# Revit family: Lighting_Pendants_Zero_Sprinkle
name_source: partatom
category: Lighting Fixtures
units: mm (PartAtom-declared; Revit-internal decimal feet)

## family parameters
Always vertical = Yes
Cut with Voids When Loaded = No
Light Source = Yes
OmniClass Number = 23.80.70.00
OmniClass Title = Lighting
Part Type = Normal
Room Calculation Point = No
Round Connector Dimension = Use Diameter
Shared = No
Work Plane-Based = No

## types (6) — shared parameters
AssetType = Fixed
BIMObjectName = Lighting_Pendants_Zero_Sprinkle
Brand = Zero
Category = Luminaires
Collection = Sprinkle
Color = Various
Color Filter = 16777215
Designer = Note Design Studio 2022
Dimming Lamp Color Temperature Shift = <None>
DurationUnit = Hours
ElectricalDeviceNominalPower = 4.9
Emit Shape Visible in Rendering = No
Emit from Circle Diameter = 120 mm  [stored 0.393701 ft]
Features = LED info: Including dimmable Led lightsource 4,9W,6,2W/GU10 CRI 90.
Finish = Aluminum and steel. Painted oysterwhite RAL 1013, black RAL 9005, blue RAL 2806035, red RAL 1013, ochre yellow RAL 1024, brown RAL 070420.
Other colours on request. Textile cord in matching colour.
HasProtectiveEarth = No
IP_Code = IP 20
IfcExportAs = IfcLightFixtureType
IfcExportType = NOTDEFINED
LensMaterial = Mat Acrylic
LightFixtureMountingType = Suspended
LightFixturePlacingType = Ceilling
Manufacturer = Zero
ManufacturerName = Zero
ManufacturerURL = https://www.zerolighting.com
Material = Aluminium&Steel
Model = Sprinkle Pendant
NBSDescription = General purpose luminaires
NBSReference = 90-60-50/405
Name = Zero_Sprinkle
NominalFrequencyRange = 50 Hz
NominalHeight = 540 mm
NominalLength = 120 mm  [stored 0.393701 ft]
NominalVoltage = 230 V
NominalVoltageCalc = 230 V
NominalWidth = 120 mm  [stored 0.393701 ft]
NumberOfPoles = 1
Photometric Web File = Sprinkle-123001-4,9W.IES
ProductDatasheet = https://www.zerolighting.com
Revision = 1
Shape = Sculptured
Size = 120x120x540 mm
Tilt Angle = 90.00°
TotalWattage = 5 W
URL = https://www.zerolighting.com
Uniclass2 = Pr_70_70_49_43
Uniclass2015Description = Light-emitting diode (LED) luminaires
Uniclass2015Reference = Pr_70_70_48_46
Version = 2
VersionDate = 31/08/2023
zero-valued in all types: Default Elevation, DefaultElevation, NumberOfSources

## per-type parameters (varying)
| type | Article Number | LightFixtureMainMaterial | ModelNumber |
| Sprinkle - Oyster white Max 7W/GU10 | 12300109 | Oyster white RAL 1013 | 12300109 |
| Sprinkle - Black 4,9W/GU10/355LM | 12300106 | Black RAL 9005 | 12300106 |
| Sprinkle - Red 4,9W/GU10/355LM | 12300107 | Red RAL 3000 | 12300107 |
| Sprinkle - Blue 4,9W/GU10/355LM | 12300108 | Blue RAL 2806035 | 12300108 |
| Sprinkle - Brown 4,9W/GU10/355LM | 12300145 | Brown RAL 070420 | 12300145 |
| Sprinkle - Ochre yellow 4,9W/GU10/355LM | 12300155 | Ochre yellow RAL 1024 | 12300155 |

note: [stored X ft] marks values corroborated as IEEE doubles in the binary element streams (Revit-internal decimal feet)

## geometry (parser evidence)
native form markers: Sweep x4
no freeform markers — native parametric forms only
